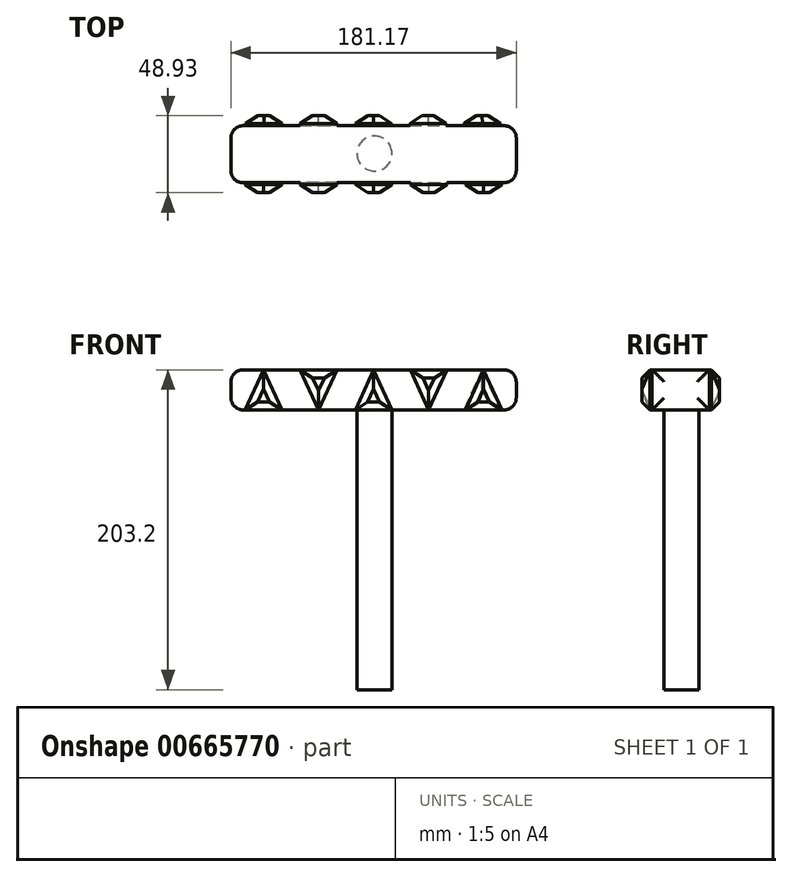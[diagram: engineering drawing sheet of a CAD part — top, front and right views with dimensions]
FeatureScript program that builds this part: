
annotation { "Feature Type Name" : "Feature", "Feature Type Description" : "" }
export const myFeature = defineFeature(function(context is Context, id is Id, definition is map)
    precondition{}
    {
        {
            var Q0;
            Q0=qCreatedBy(makeId("Top.planeOp"),FACE);
            var sketch = newSketch(context, id + "F0", { "sketchPlane" : qUnion([Q0])});
            skLineSegment(sketch, "E0.bottom", {"start": v(-40.34, -18.56) * mm, "end": v(39.23, -18.56) * mm});
            skLineSegment(sketch, "E0.top", {"start": v(-40.34, 17.67) * mm, "end": v(39.23, 17.67) * mm});
            skLineSegment(sketch, "E0.left", {"start": v(-40.34, -18.56) * mm, "end": v(-40.34, 17.67) * mm});
            skLineSegment(sketch, "E0.right", {"start": v(39.23, -18.56) * mm, "end": v(39.23, 17.67) * mm});
            skSolve(sketch);
        }
        {
            var Q0;
            Q0=makeQuery(id+"F0.imprint","IMPRINT",FACE,{"disambiguationData":[TD([[makeQuery(id+"F0.imprint","IMPRINT",EDGE,{"derivedFrom":sQuery(id+"F0.wireOp",EDGE,"E0.bottom")}),1.0]])]});
            extrude(context, id + "F1", {"entities" : qUnion([Q0]), "depth" : 12.7 * mm, "offsetDistance" : 25.4 * mm});
        }
        {
            var Q0;
            Q0=makeQuery(id+"F1.opExtrude","CAP_FACE",FACE,{"disambiguationData":[OSD([sQuery(id+"F0.wireOp",EDGE,"E0.bottom"),sQuery(id+"F0.wireOp",EDGE,"E0.top"),sQuery(id+"F0.wireOp",EDGE,"E0.left"),sQuery(id+"F0.wireOp",EDGE,"E0.right")])],"isStart":true});
            extrude(context, id + "F2", {"entities" : qUnion([Q0]), "operationType" : NewBodyOperationType.ADD, "depth" : 12.7 * mm, "offsetDistance" : 25.4 * mm});
        }
        {
            var Q0;
            Q0=makeQuery(id+"F2.opExtrude","CAP_FACE",FACE,{"disambiguationData":[OSD([sQuery(id+"F0.wireOp",EDGE,"E0.bottom"),sQuery(id+"F0.wireOp",EDGE,"E0.top"),sQuery(id+"F0.wireOp",EDGE,"E0.left"),sQuery(id+"F0.wireOp",EDGE,"E0.right")])],"isStart":false});
            var sketch = newSketch(context, id + "F3", { "sketchPlane" : qUnion([Q0])});
            skCircle(sketch, "E1", {"center": v(0, 0) * mm, "radius": 11.13 * mm});
            skSolve(sketch);
        }
        {
            var Q0;
            Q0=makeQuery(id+"F3.imprint","IMPRINT",FACE,{"disambiguationData":[TD([[makeQuery(id+"F3.imprint","IMPRINT",EDGE,{"derivedFrom":sQuery(id+"F3.wireOp",EDGE,"E1")}),1.0]])]});
            extrude(context, id + "F4", {"entities" : qUnion([Q0]), "operationType" : NewBodyOperationType.ADD, "depth" : 177.8 * mm, "offsetDistance" : 25.4 * mm});
        }
        {
            var Q0;
            Q0=makeQuery(id+"F1.opExtrude","CAP_FACE",FACE,{"disambiguationData":[OSD([sQuery(id+"F0.wireOp",EDGE,"E0.bottom"),sQuery(id+"F0.wireOp",EDGE,"E0.top"),sQuery(id+"F0.wireOp",EDGE,"E0.left"),sQuery(id+"F0.wireOp",EDGE,"E0.right")])],"isStart":false});
            var sketch = newSketch(context, id + "F5", { "sketchPlane" : qUnion([Q0])});
            skLineSegment(sketch, "E2", {"start": v(0, -17.92) * mm, "end": v(-39.6, 0) * mm});
            skLineSegment(sketch, "E3", {"start": v(0, -17.92) * mm, "end": v(38.59, 0) * mm});
            skLineSegment(sketch, "E4", {"start": v(38.59, 0) * mm, "end": v(0, 17) * mm});
            skLineSegment(sketch, "E5", {"start": v(-39.6, 0) * mm, "end": v(0, 17) * mm});
            skSolve(sketch);
        }
        {
            var Q0;
            Q0=makeQuery(id+"FtfhKkzBTMOApFl_1.opExtrude","CAP_FACE",FACE,{"disambiguationData":[OSD([sQuery(id+"F5.wireOp",EDGE,"E2"),sQuery(id+"F5.wireOp",EDGE,"E3"),sQuery(id+"F5.wireOp",EDGE,"E4"),sQuery(id+"F5.wireOp",EDGE,"E5")])],"isStart":false});
            var sketch = newSketch(context, id + "F6", { "sketchPlane" : qUnion([Q0])});
            skSolve(sketch);
        }
        {
            var Q0;
            {var subQ0=sQuery(id+"F0.wireOp",EDGE,"E0.left");Q0=makeQuery(id+"F2.boolean.opBoolean","MERGE",FACE,{"derivedFrom":[makeQuery(id+"F1.opExtrude","SWEPT_FACE",FACE,{"disambiguationData":[OSD([subQ0])]}),makeQuery(id+"F2.opExtrude","SWEPT_FACE",FACE,{"disambiguationData":[OSD([subQ0])]})]});}
            extrude(context, id + "F7", {"entities" : qUnion([Q0]), "operationType" : NewBodyOperationType.ADD, "depth" : 50.8 * mm, "offsetDistance" : 25.4 * mm});
        }
        {
            var Q0;
            {var subQ0=sQuery(id+"F0.wireOp",EDGE,"E0.right");Q0=makeQuery(id+"F2.boolean.opBoolean","MERGE",FACE,{"derivedFrom":[makeQuery(id+"F1.opExtrude","SWEPT_FACE",FACE,{"disambiguationData":[OSD([subQ0])]}),makeQuery(id+"F2.opExtrude","SWEPT_FACE",FACE,{"disambiguationData":[OSD([subQ0])]})]});}
            extrude(context, id + "F8", {"entities" : qUnion([Q0]), "operationType" : NewBodyOperationType.ADD, "depth" : 50.8 * mm, "offsetDistance" : 25.4 * mm});
        }
        {
            var Q0;
            {var subQ0=sQuery(id+"F0.wireOp",EDGE,"E0.bottom");Q0=makeQuery(id+"F8.boolean.opBoolean","MERGE",FACE,{"derivedFrom":[makeQuery(id+"F7.boolean.opBoolean","MERGE",FACE,{"derivedFrom":[makeQuery(id+"F2.boolean.opBoolean","MERGE",FACE,{"derivedFrom":[makeQuery(id+"F1.opExtrude","SWEPT_FACE",FACE,{"disambiguationData":[OSD([subQ0])]}),makeQuery(id+"F2.opExtrude","SWEPT_FACE",FACE,{"disambiguationData":[OSD([subQ0])]})]}),makeQuery(id+"F7.opExtrude","SWEPT_FACE",FACE,{"disambiguationData":[OSD([subQ0,sQuery(id+"F0.wireOp",EDGE,"E0.left")])]})]}),makeQuery(id+"F8.opExtrude","SWEPT_FACE",FACE,{"disambiguationData":[OSD([subQ0,sQuery(id+"F0.wireOp",EDGE,"E0.right")])]})]});}
            var sketch = newSketch(context, id + "F9", { "sketchPlane" : qUnion([Q0])});
            skLineSegment(sketch, "E6", {"start": v(-0.56, 12.7) * mm, "end": v(11.1, -12.7) * mm});
            skLineSegment(sketch, "E7", {"start": v(-0.56, 12.7) * mm, "end": v(-12.2, -12.7) * mm});
            skLineSegment(sketch, "E8", {"start": v(-12.2, -12.7) * mm, "end": v(-23.85, 12.7) * mm});
            skLineSegment(sketch, "E9", {"start": v(-23.85, 12.7) * mm, "end": v(-35.5, -12.7) * mm});
            skLineSegment(sketch, "E10", {"start": v(11.1, -12.7) * mm, "end": v(22.74, 12.7) * mm});
            skLineSegment(sketch, "E11", {"start": v(22.74, 12.7) * mm, "end": v(34.39, -12.7) * mm});
            skLineSegment(sketch, "E12", {"start": v(34.39, -12.7) * mm, "end": v(46.03, 12.7) * mm});
            skLineSegment(sketch, "E13", {"start": v(46.03, 12.7) * mm, "end": v(57.68, -12.7) * mm});
            skLineSegment(sketch, "E14", {"start": v(57.68, -12.7) * mm, "end": v(69.32, 12.7) * mm});
            skLineSegment(sketch, "E15", {"start": v(69.32, 12.7) * mm, "end": v(80.97, -12.7) * mm});
            skLineSegment(sketch, "E16", {"start": v(80.97, -12.7) * mm, "end": v(90.03, 7.05) * mm});
            skLineSegment(sketch, "E17", {"start": v(-35.5, -12.7) * mm, "end": v(-47.14, 12.7) * mm});
            skLineSegment(sketch, "E18", {"start": v(-47.14, 12.7) * mm, "end": v(-58.79, -12.7) * mm});
            skLineSegment(sketch, "E19", {"start": v(-58.79, -12.7) * mm, "end": v(-70.44, 12.7) * mm});
            skLineSegment(sketch, "E20", {"start": v(-70.44, 12.7) * mm, "end": v(-82.08, -12.7) * mm});
            skLineSegment(sketch, "E21", {"start": v(-82.08, -12.7) * mm, "end": v(-91.14, 7.05) * mm});
            skSolve(sketch);
        }
        {
            var Q0;
            {var subQ0=sQuery(id+"F0.wireOp",EDGE,"E0.top");Q0=makeQuery(id+"F8.boolean.opBoolean","MERGE",FACE,{"derivedFrom":[makeQuery(id+"F7.boolean.opBoolean","MERGE",FACE,{"derivedFrom":[makeQuery(id+"F2.boolean.opBoolean","MERGE",FACE,{"derivedFrom":[makeQuery(id+"F1.opExtrude","SWEPT_FACE",FACE,{"disambiguationData":[OSD([subQ0])]}),makeQuery(id+"F2.opExtrude","SWEPT_FACE",FACE,{"disambiguationData":[OSD([subQ0])]})]}),makeQuery(id+"F7.opExtrude","SWEPT_FACE",FACE,{"disambiguationData":[OSD([subQ0,sQuery(id+"F0.wireOp",EDGE,"E0.left")])]})]}),makeQuery(id+"F8.opExtrude","SWEPT_FACE",FACE,{"disambiguationData":[OSD([subQ0,sQuery(id+"F0.wireOp",EDGE,"E0.right")])]})]});}
            var sketch = newSketch(context, id + "F10", { "sketchPlane" : qUnion([Q0])});
            skLineSegment(sketch, "E22", {"start": v(0.56, 12.7) * mm, "end": v(12.1, -12.7) * mm});
            skLineSegment(sketch, "E23", {"start": v(12.1, -12.7) * mm, "end": v(23.69, 12.7) * mm});
            skLineSegment(sketch, "E24", {"start": v(23.69, 12.7) * mm, "end": v(35.54, -12.7) * mm});
            skLineSegment(sketch, "E25", {"start": v(35.54, -12.7) * mm, "end": v(47.26, 12.7) * mm});
            skLineSegment(sketch, "E26", {"start": v(47.26, 12.7) * mm, "end": v(58.85, -12.7) * mm});
            skLineSegment(sketch, "E27", {"start": v(58.85, -12.7) * mm, "end": v(70.3, 12.7) * mm});
            skLineSegment(sketch, "E28", {"start": v(70.3, 12.7) * mm, "end": v(81.84, -12.7) * mm});
            skLineSegment(sketch, "E29", {"start": v(81.84, -12.7) * mm, "end": v(91.14, 7.45) * mm});
            skLineSegment(sketch, "E30", {"start": v(0.56, 12.7) * mm, "end": v(-10.9, -12.7) * mm});
            skLineSegment(sketch, "E31", {"start": v(-10.9, -12.7) * mm, "end": v(-22.44, 12.7) * mm});
            skLineSegment(sketch, "E32", {"start": v(-22.44, 12.7) * mm, "end": v(-33.89, -12.7) * mm});
            skLineSegment(sketch, "E33", {"start": v(-33.89, -12.7) * mm, "end": v(-45.44, 12.7) * mm});
            skLineSegment(sketch, "E34", {"start": v(-45.44, 12.7) * mm, "end": v(-56.89, -12.7) * mm});
            skLineSegment(sketch, "E35", {"start": v(-56.89, -12.7) * mm, "end": v(-68.44, 12.7) * mm});
            skLineSegment(sketch, "E36", {"start": v(-68.44, 12.7) * mm, "end": v(-79.88, -12.7) * mm});
            skLineSegment(sketch, "E37", {"start": v(-79.88, -12.7) * mm, "end": v(-90.03, 6.92) * mm});
            skSolve(sketch);
        }
        {
            var Q0;
            {var subQ0=sQuery(id+"F9.wireOp",EDGE,"E6");Q0=makeQuery(id+"F9.imprint","IMPRINT",FACE,{"disambiguationData":[TD([[makeQuery(id+"F9.imprint","IMPRINT",EDGE,{"derivedFrom":subQ0}),-1.0]])]});}
            var Q1;
            {var subQ0=sQuery(id+"F9.wireOp",EDGE,"E11");Q1=makeQuery(id+"F9.imprint","IMPRINT",FACE,{"disambiguationData":[TD([[makeQuery(id+"F9.imprint","IMPRINT",EDGE,{"derivedFrom":subQ0}),1.0]])]});}
            var Q2;
            {var subQ0=sQuery(id+"F9.wireOp",EDGE,"E14");Q2=makeQuery(id+"F9.imprint","IMPRINT",FACE,{"disambiguationData":[TD([[makeQuery(id+"F9.imprint","IMPRINT",EDGE,{"derivedFrom":subQ0}),-1.0]])]});}
            var Q3;
            {var subQ0=sQuery(id+"F9.wireOp",EDGE,"E9");Q3=makeQuery(id+"F9.imprint","IMPRINT",FACE,{"disambiguationData":[TD([[makeQuery(id+"F9.imprint","IMPRINT",EDGE,{"derivedFrom":subQ0}),-1.0]])]});}
            var Q4;
            {var subQ0=sQuery(id+"F9.wireOp",EDGE,"E19");Q4=makeQuery(id+"F9.imprint","IMPRINT",FACE,{"disambiguationData":[TD([[makeQuery(id+"F9.imprint","IMPRINT",EDGE,{"derivedFrom":subQ0}),1.0]])]});}
            extrude(context, id + "F11", {"entities" : qUnion([Q0, Q1, Q2, Q3, Q4]), "operationType" : NewBodyOperationType.ADD, "depth" : 6.35 * mm, "offsetDistance" : 25.4 * mm});
        }
        {
            var Q0;
            Q0=makeQuery(id+"F11.opExtrude","CAP_FACE",FACE,{"disambiguationData":[OSD([sQuery(id+"F0.wireOp",EDGE,"E0.bottom"),sQuery(id+"F0.wireOp",EDGE,"E0.left"),sQuery(id+"F0.wireOp",EDGE,"E0.right"),sQuery(id+"F9.wireOp",EDGE,"E19"),sQuery(id+"F9.wireOp",EDGE,"E20")])],"isStart":false});
            var Q1;
            Q1=makeQuery(id+"F11.opExtrude","CAP_FACE",FACE,{"disambiguationData":[OSD([sQuery(id+"F0.wireOp",EDGE,"E0.bottom"),sQuery(id+"F0.wireOp",EDGE,"E0.left"),sQuery(id+"F0.wireOp",EDGE,"E0.right"),sQuery(id+"F9.wireOp",EDGE,"E9"),sQuery(id+"F9.wireOp",EDGE,"E17")])],"isStart":false});
            var Q2;
            Q2=makeQuery(id+"F11.opExtrude","CAP_FACE",FACE,{"disambiguationData":[OSD([sQuery(id+"F0.wireOp",EDGE,"E0.bottom"),sQuery(id+"F0.wireOp",EDGE,"E0.left"),sQuery(id+"F0.wireOp",EDGE,"E0.right"),sQuery(id+"F9.wireOp",EDGE,"E6"),sQuery(id+"F9.wireOp",EDGE,"E7")])],"isStart":false});
            var Q3;
            Q3=makeQuery(id+"F11.opExtrude","CAP_FACE",FACE,{"disambiguationData":[OSD([sQuery(id+"F0.wireOp",EDGE,"E0.bottom"),sQuery(id+"F0.wireOp",EDGE,"E0.left"),sQuery(id+"F0.wireOp",EDGE,"E0.right"),sQuery(id+"F9.wireOp",EDGE,"E11"),sQuery(id+"F9.wireOp",EDGE,"E12")])],"isStart":false});
            var Q4;
            Q4=makeQuery(id+"F11.opExtrude","CAP_FACE",FACE,{"disambiguationData":[OSD([sQuery(id+"F0.wireOp",EDGE,"E0.bottom"),sQuery(id+"F0.wireOp",EDGE,"E0.left"),sQuery(id+"F0.wireOp",EDGE,"E0.right"),sQuery(id+"F9.wireOp",EDGE,"E14"),sQuery(id+"F9.wireOp",EDGE,"E15")])],"isStart":false});
            chamfer(context, id + "F12", {"entities" : qUnion([Q0, Q1, Q2, Q3, Q4]), "width" : 5.08 * mm, "tangentPropagation" : true});
        }
        {
            var Q0;
            {var subQ0=sQuery(id+"F10.wireOp",EDGE,"E22");Q0=makeQuery(id+"F10.imprint","IMPRINT",FACE,{"disambiguationData":[TD([[makeQuery(id+"F10.imprint","IMPRINT",EDGE,{"derivedFrom":subQ0}),-1.0]])]});}
            var Q1;
            {var subQ0=sQuery(id+"F10.wireOp",EDGE,"E24");Q1=makeQuery(id+"F10.imprint","IMPRINT",FACE,{"disambiguationData":[TD([[makeQuery(id+"F10.imprint","IMPRINT",EDGE,{"derivedFrom":subQ0}),1.0]])]});}
            var Q2;
            {var subQ0=sQuery(id+"F10.wireOp",EDGE,"E27");Q2=makeQuery(id+"F10.imprint","IMPRINT",FACE,{"disambiguationData":[TD([[makeQuery(id+"F10.imprint","IMPRINT",EDGE,{"derivedFrom":subQ0}),-1.0]])]});}
            var Q3;
            {var subQ0=sQuery(id+"F10.wireOp",EDGE,"E32");Q3=makeQuery(id+"F10.imprint","IMPRINT",FACE,{"disambiguationData":[TD([[makeQuery(id+"F10.imprint","IMPRINT",EDGE,{"derivedFrom":subQ0}),-1.0]])]});}
            var Q4;
            {var subQ0=sQuery(id+"F10.wireOp",EDGE,"E35");Q4=makeQuery(id+"F10.imprint","IMPRINT",FACE,{"disambiguationData":[TD([[makeQuery(id+"F10.imprint","IMPRINT",EDGE,{"derivedFrom":subQ0}),1.0]])]});}
            extrude(context, id + "F13", {"entities" : qUnion([Q0, Q1, Q2, Q3, Q4]), "operationType" : NewBodyOperationType.ADD, "depth" : 6.35 * mm, "offsetDistance" : 25.4 * mm});
        }
        {
            var Q0;
            Q0=makeQuery(id+"F13.opExtrude","CAP_FACE",FACE,{"disambiguationData":[OSD([sQuery(id+"F0.wireOp",EDGE,"E0.top"),sQuery(id+"F0.wireOp",EDGE,"E0.left"),sQuery(id+"F0.wireOp",EDGE,"E0.right"),sQuery(id+"F10.wireOp",EDGE,"E35"),sQuery(id+"F10.wireOp",EDGE,"E36")])],"isStart":false});
            var Q1;
            Q1=makeQuery(id+"F13.opExtrude","CAP_FACE",FACE,{"disambiguationData":[OSD([sQuery(id+"F0.wireOp",EDGE,"E0.top"),sQuery(id+"F0.wireOp",EDGE,"E0.left"),sQuery(id+"F0.wireOp",EDGE,"E0.right"),sQuery(id+"F10.wireOp",EDGE,"E32"),sQuery(id+"F10.wireOp",EDGE,"E33")])],"isStart":false});
            var Q2;
            Q2=makeQuery(id+"F13.opExtrude","CAP_FACE",FACE,{"disambiguationData":[OSD([sQuery(id+"F0.wireOp",EDGE,"E0.top"),sQuery(id+"F0.wireOp",EDGE,"E0.left"),sQuery(id+"F0.wireOp",EDGE,"E0.right"),sQuery(id+"F10.wireOp",EDGE,"E22"),sQuery(id+"F10.wireOp",EDGE,"E30")])],"isStart":false});
            var Q3;
            Q3=makeQuery(id+"F13.opExtrude","CAP_FACE",FACE,{"disambiguationData":[OSD([sQuery(id+"F0.wireOp",EDGE,"E0.top"),sQuery(id+"F0.wireOp",EDGE,"E0.left"),sQuery(id+"F0.wireOp",EDGE,"E0.right"),sQuery(id+"F10.wireOp",EDGE,"E24"),sQuery(id+"F10.wireOp",EDGE,"E25")])],"isStart":false});
            var Q4;
            Q4=makeQuery(id+"F13.opExtrude","CAP_FACE",FACE,{"disambiguationData":[OSD([sQuery(id+"F0.wireOp",EDGE,"E0.top"),sQuery(id+"F0.wireOp",EDGE,"E0.left"),sQuery(id+"F0.wireOp",EDGE,"E0.right"),sQuery(id+"F10.wireOp",EDGE,"E27"),sQuery(id+"F10.wireOp",EDGE,"E28")])],"isStart":false});
            chamfer(context, id + "F14", {"entities" : qUnion([Q0, Q1, Q2, Q3, Q4]), "width" : 5.08 * mm, "tangentPropagation" : true});
        }
        {
            var Q0;
            Q0=makeQuery(id+"F8.opExtrude","CAP_FACE",FACE,{"disambiguationData":[OSD([sQuery(id+"F0.wireOp",EDGE,"E0.right")])],"isStart":false});
            fillet(context, id + "F15", {"entities" : qUnion([Q0]), "radius" : 7.62 * mm, "tangentPropagation" : true, "allowEdgeOverflow" : false});
        }
        {
            var Q0;
            Q0=makeQuery(id+"F7.opExtrude","CAP_FACE",FACE,{"disambiguationData":[OSD([sQuery(id+"F0.wireOp",EDGE,"E0.left")])],"isStart":false});
            fillet(context, id + "F16", {"entities" : qUnion([Q0]), "radius" : 7.62 * mm, "tangentPropagation" : true, "allowEdgeOverflow" : false});
        }
    });
